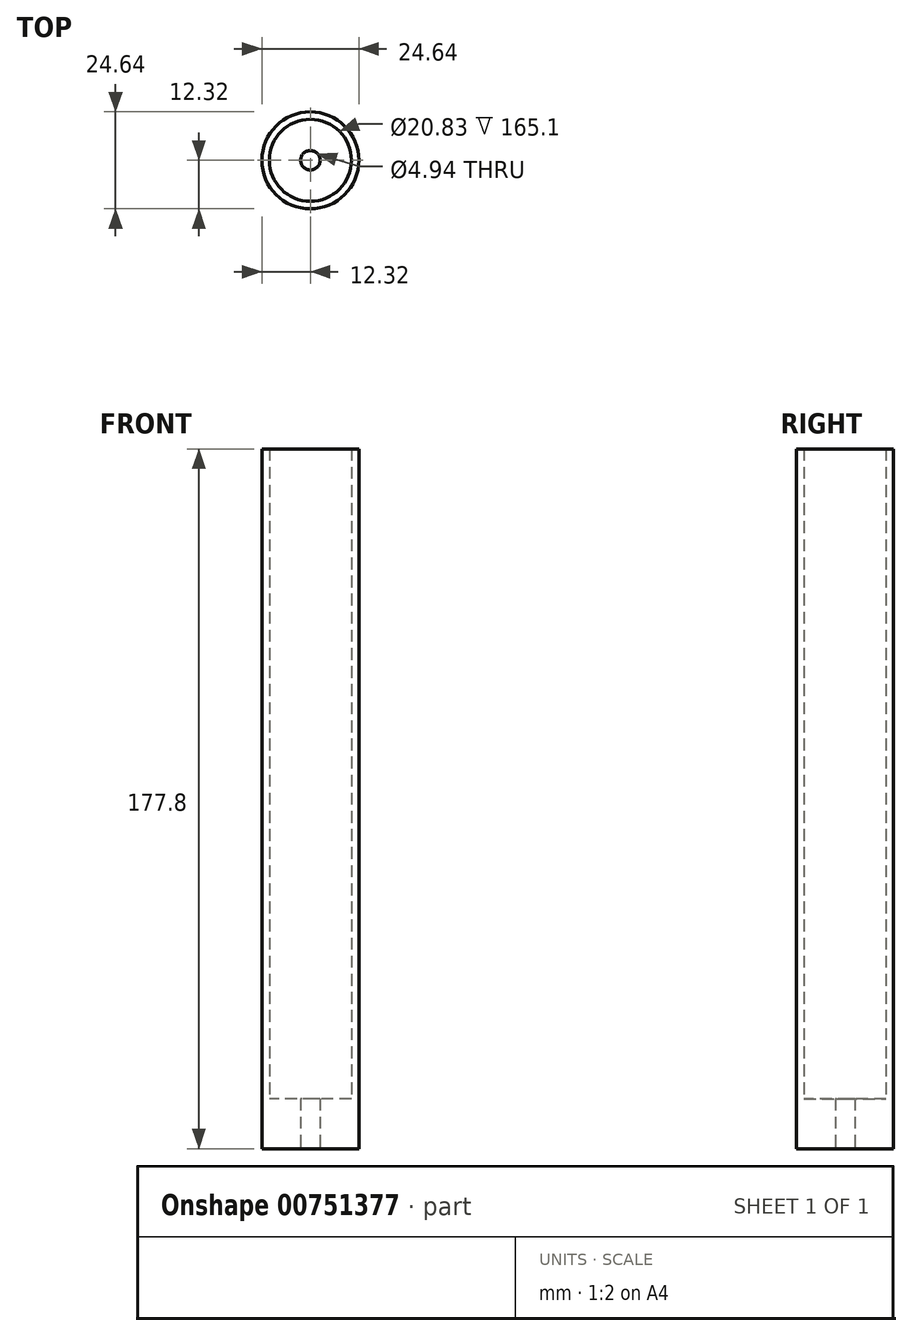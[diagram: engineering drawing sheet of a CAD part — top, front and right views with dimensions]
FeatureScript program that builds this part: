
annotation { "Feature Type Name" : "Feature", "Feature Type Description" : "" }
export const myFeature = defineFeature(function(context is Context, id is Id, definition is map)
    precondition{}
    {
        {
            var Q0;
            Q0=qCreatedBy(makeId("Top.planeOp"),FACE);
            var sketch = newSketch(context, id + "F0", { "sketchPlane" : qUnion([Q0])});
            skCircle(sketch, "E0.0", {"center": v(0, 0) * mm, "radius": 12.32 * mm});
            skCircle(sketch, "E1.0", {"center": v(0, 0) * mm, "radius": 10.41 * mm});
            skCircle(sketch, "E2", {"center": v(0, 0) * mm, "radius": 2.47 * mm});
            skSolve(sketch);
        }
        {
            var Q0;
            Q0=makeQuery(id+"F0.imprint","IMPRINT",FACE,{"disambiguationData":[TD([[makeQuery(id+"F0.imprint","IMPRINT",EDGE,{"derivedFrom":sQuery(id+"F0.wireOp",EDGE,"E0.0")}),1.0]])]});
            var Q1;
            Q1=sQuery(id+"F0.wireOp",EDGE,"E0.0");
            var Q2;
            Q2=sQuery(id+"F0.wireOp",EDGE,"E1.0");
            extrude(context, id + "F1", {"entities" : qUnion([Q0]), "surfaceEntities" : qUnion([Q1, Q2]), "depth" : 177.8 * mm, "offsetDistance" : 25.4 * mm});
        }
        {
            var Q0;
            Q0=makeQuery(id+"F0.imprint","IMPRINT",FACE,{"disambiguationData":[TD([[makeQuery(id+"F0.imprint","IMPRINT",EDGE,{"derivedFrom":sQuery(id+"F0.wireOp",EDGE,"E1.0")}),1.0]])]});
            extrude(context, id + "F2", {"entities" : qUnion([Q0]), "operationType" : NewBodyOperationType.ADD, "depth" : 12.7 * mm, "offsetDistance" : 25.4 * mm});
        }
        {
            var Q0;
            Q0=makeQuery(id+"F0.imprint","IMPRINT",FACE,{"disambiguationData":[TD([[makeQuery(id+"F0.imprint","IMPRINT",EDGE,{"derivedFrom":sQuery(id+"F0.wireOp",EDGE,"E2")}),1.0]])]});
            extrude(context, id + "F3", {"entities" : qUnion([Q0]), "operationType" : NewBodyOperationType.REMOVE, "oppositeDirection" : true, "depth" : 25.4 * mm, "offsetDistance" : 25.4 * mm});
        }
    });
